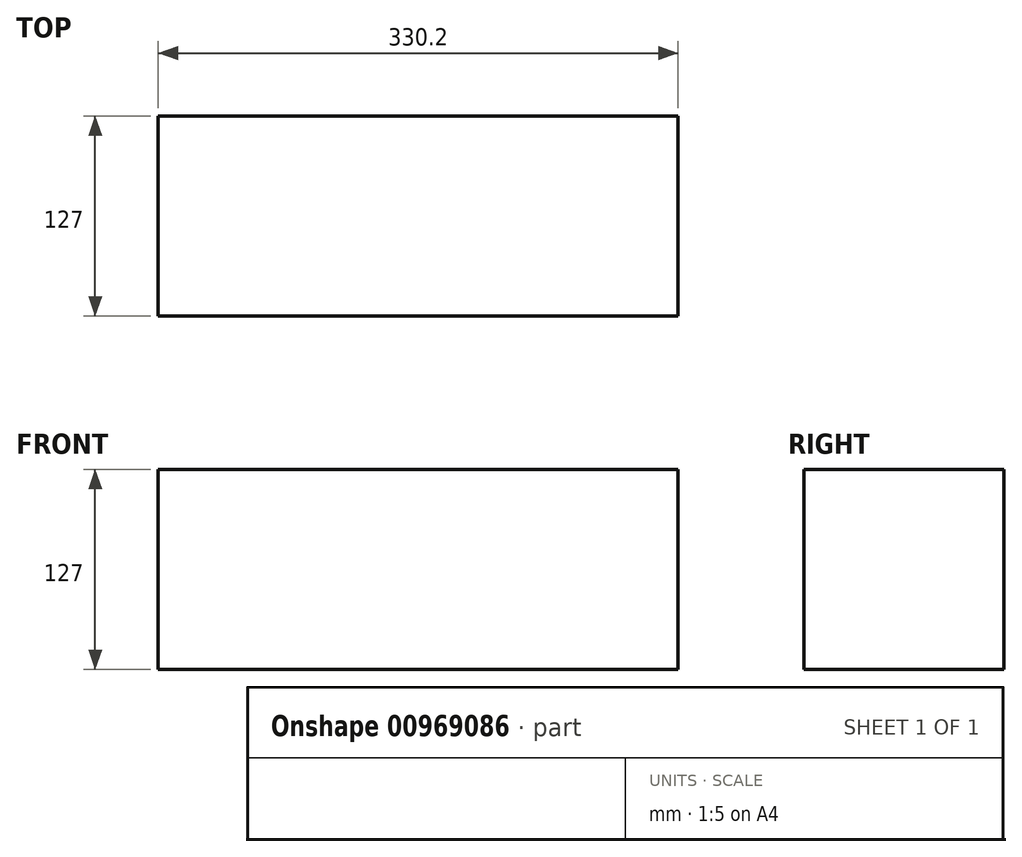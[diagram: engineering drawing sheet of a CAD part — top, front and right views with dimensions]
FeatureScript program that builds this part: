
annotation { "Feature Type Name" : "Feature", "Feature Type Description" : "" }
export const myFeature = defineFeature(function(context is Context, id is Id, definition is map)
    precondition{}
    {
        {
            var Q0;
            Q0=qCreatedBy(makeId("Top.planeOp"),FACE);
            var sketch = newSketch(context, id + "F0", { "sketchPlane" : qUnion([Q0])});
            skLineSegment(sketch, "E0.bottom", {"start": v(0, 0) * mm, "end": v(330.2, 0) * mm});
            skLineSegment(sketch, "E0.top", {"start": v(0, 127) * mm, "end": v(330.2, 127) * mm});
            skLineSegment(sketch, "E0.left", {"start": v(0, 0) * mm, "end": v(0, 127) * mm});
            skLineSegment(sketch, "E0.right", {"start": v(330.2, 0) * mm, "end": v(330.2, 127) * mm});
            skSolve(sketch);
        }
        {
            var Q0;
            Q0 = qSketchRegion(id + "F0", true);
            extrude(context, id + "F1", {"entities" : qUnion([Q0]), "depth" : 127 * mm, "offsetDistance" : 25.4 * mm});
        }
    });
